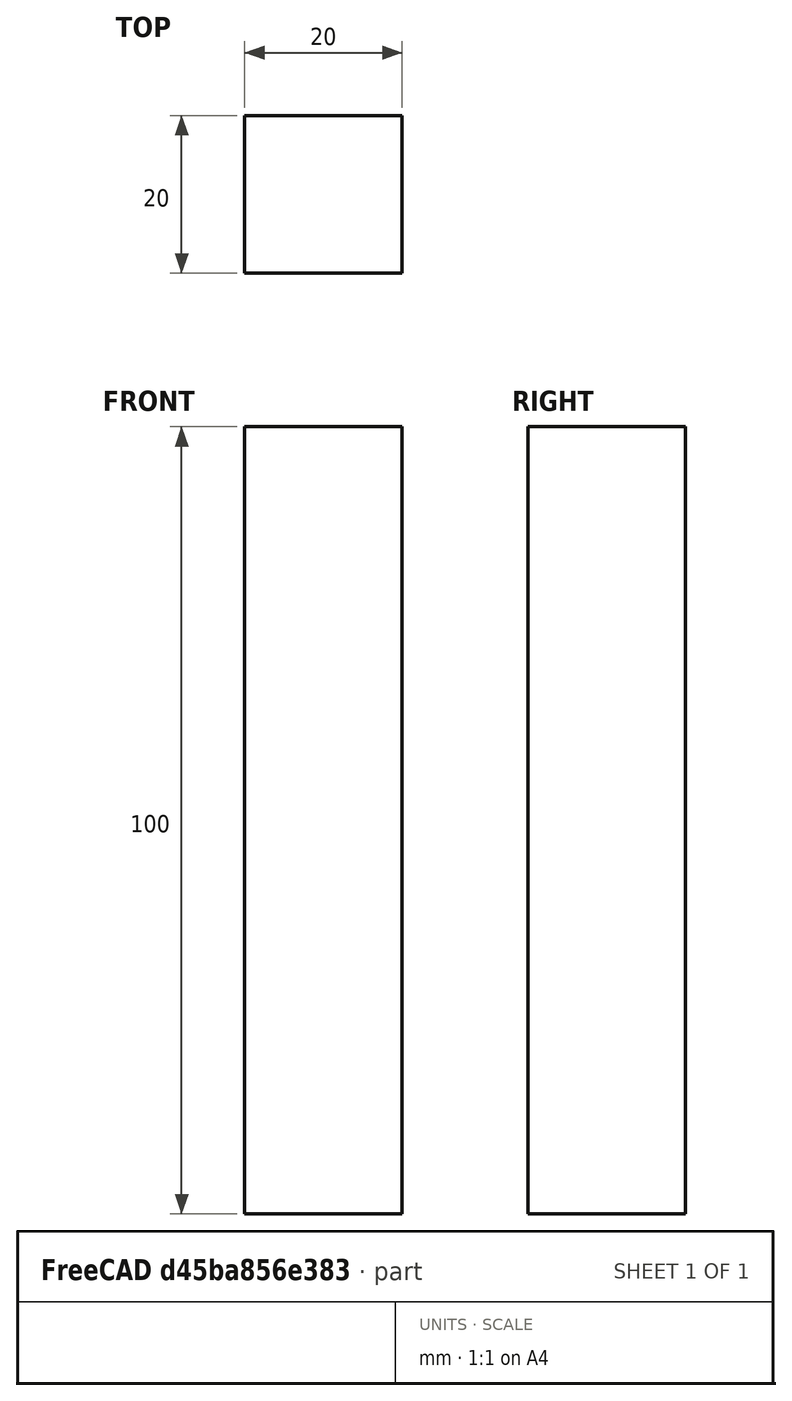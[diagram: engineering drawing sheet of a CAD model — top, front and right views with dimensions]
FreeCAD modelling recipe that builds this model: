
FCSTD DOCUMENT  (FreeCAD 0.19R24291 (Git))
Label: Sigma Profil
License: All rights reserved
LicenseURL: http://en.wikipedia.org/wiki/All_rights_reserved
objects: Sketcher::SketchObject×2, PartDesign::Pad×1, PartDesign::Body×1
note: 5 computed .brp shape members not serialized (recipe doc carries the construction recipe); baked Part::Feature solids carry a one-line shape summary decoded from their .brp

FEATURE [Sketcher::SketchObject] Sketch
  FullyConstrained = true
  MapMode = 5
  Support = -> [XY_Plane]
  sketch-geometry (4):
    g0: LineSegment StartX=-10 StartY=10 StartZ=0 EndX=10 EndY=10 EndZ=0
    g1: LineSegment StartX=10 StartY=10 StartZ=0 EndX=10 EndY=-10 EndZ=0
    g2: LineSegment StartX=10 StartY=-10 StartZ=0 EndX=-10 EndY=-10 EndZ=0
    g3: LineSegment StartX=-10 StartY=-10 StartZ=0 EndX=-10 EndY=10 EndZ=0
  constraints (12):
    c: Coincident(g0,g1)
    c: Coincident(g1,g2)
    c: Coincident(g2,g3)
    c: Coincident(g3,g0)
    c: Horizontal(g0)
    c: Horizontal(g2)
    c: Vertical(g1)
    c: Vertical(g3)
    c: DistanceY(g3,g3) = 20
    c: DistanceX(g0,g0) = 20
    c: DistanceY(g-1,g0) = 10
    c: DistanceX(g-1,g0) = 10
FEATURE [PartDesign::Pad] Pad
  Direction = (1,1,1)
  Length = 100
  Length2 = 100
  Profile = -> Sketch
  Type = 0
FEATURE [Sketcher::SketchObject] Sketch001
  ExternalGeometry = -> [Pad]
  FullyConstrained = true
  MapMode = 5
  Placement = pos=(0,0,100) rot=(0,0,1;0rad)
  Support = -> [Pad]
FEATURE [PartDesign::Body] Body
  Group = -> [Sketch,Pad,Sketch001]
  Origin = -> Origin
  Tip = -> Pad
